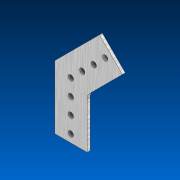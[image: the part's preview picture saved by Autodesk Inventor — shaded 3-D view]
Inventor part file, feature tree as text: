
AUTODESK INVENTOR PART (.ipt)
format: ipt  version: 2022.2 (Build 262287000, 287)  size: 145,920 bytes
history: native  units: in
note: dims shown in document units (in); Inventor stores cm internally (conversion verified against a paired STEP export)
features: extrude x1, sketch x1, projected_geometry x1, fillet x1
ambient origin geometry x8: Origin, YZ Plane, XZ Plane, XY Plane, X Axis, Y Axis, Z Axis, Center Point
bodies: Solid1 (feature_tree)
feature tree (4):
  extrude  "Extrusion1"  Depth=0.5in
  sketch  "Sketch1"  dims[d0=0.5in d1=0.5in d2=0.0in d3=0.0in]
  projected_geometry  "Projected Loop1"
  fillet  "Fillet2"  [1 undecoded]
note: 1 required parameter value undecoded (feature->parameter linkage not recoverable at this tier; creation-order binding heuristic only, values carry confidence <= 0.55)
